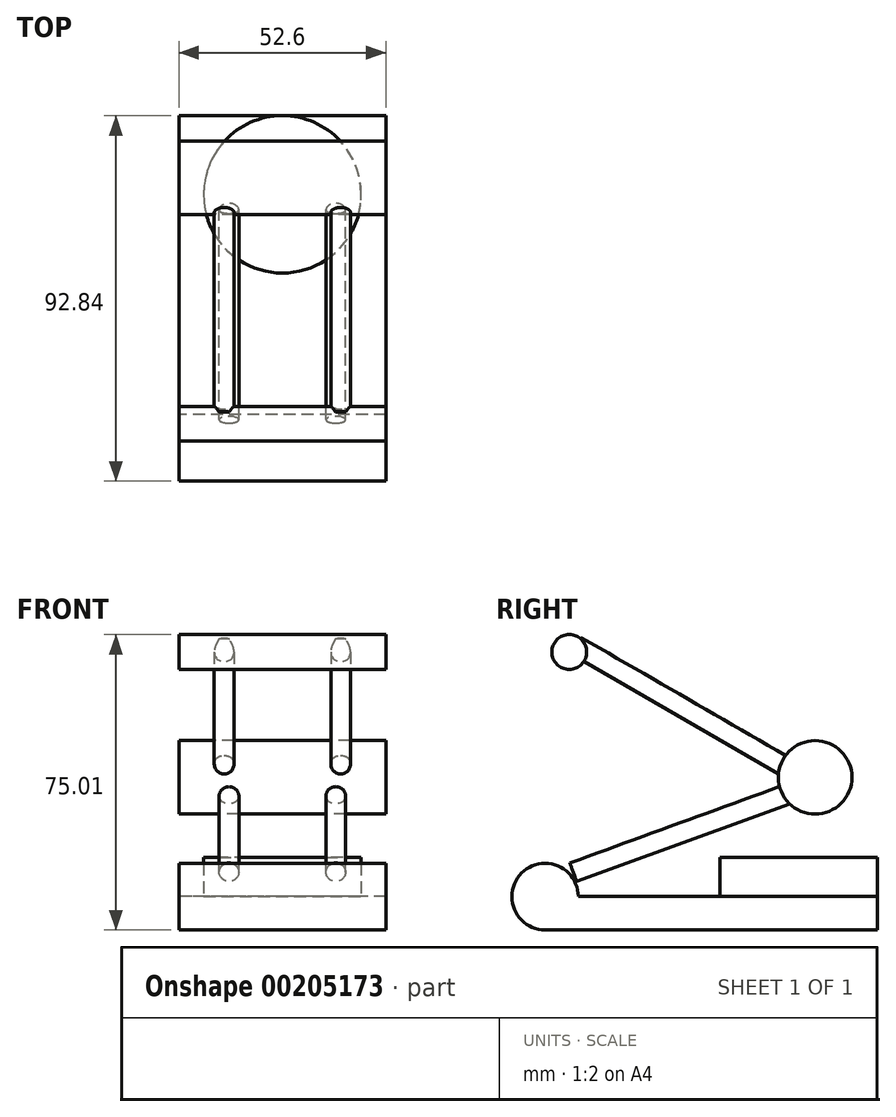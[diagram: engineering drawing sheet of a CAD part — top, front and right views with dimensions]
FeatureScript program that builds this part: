
annotation { "Feature Type Name" : "Feature", "Feature Type Description" : "" }
export const myFeature = defineFeature(function(context is Context, id is Id, definition is map)
    precondition{}
    {
        {
            var Q0;
            Q0=qCreatedBy(makeId("Right.planeOp"),FACE);
            var sketch = newSketch(context, id + "F0", { "sketchPlane" : qUnion([Q0])});
            skLineSegment(sketch, "E0", {"start": v(41.31, 0) * mm, "end": v(-34.65, 0) * mm});
            skCircle(sketch, "E1", {"center": v(25.51, 30.3) * mm, "radius": 9.34 * mm});
            skCircle(sketch, "E2", {"center": v(-36.95, 62.14) * mm, "radius": 4.43 * mm});
            skArc(sketch, "E3", {"start": v(-34.65, 0) * mm, "mid": v(-49.06, 5.97) * mm, "end": v(-43.09, -8.44) * mm});
            skLineSegment(sketch, "E4", {"start": v(41.31, 0) * mm, "end": v(41.31, -8.44) * mm});
            skLineSegment(sketch, "E5", {"start": v(41.31, -8.44) * mm, "end": v(-43.09, -8.44) * mm});
            skSolve(sketch);
        }
        {
            var Q0;
            Q0 = qSketchRegion(id + "F0", true);
            extrude(context, id + "F1", {"entities" : qUnion([Q0]), "endBound" : BoundingType.SYMMETRIC, "depth" : 52.6 * mm});
        }
        {
            var Q0;
            Q0=qCreatedBy(makeId("Front.planeOp"),FACE);
            var Q1;
            Q1=makeQuery(id+"F1.opExtrude","SWEPT_FACE",FACE,{"disambiguationData":[OSD([sQuery(id+"F0.wireOp",EDGE,"E1")])]});
            cPlane(context, id + "F2", {"entities" : qUnion([Q0, Q1]), "cplaneType" : CPlaneType.LINE_ANGLE, "offset" : 25 * mm, "angle" : 30 * degree, "width" : 150 * mm, "height" : 150 * mm});
        }
        {
            var Q0;
            Q0=qCreatedBy(id+"F2.planeOp",FACE);
            var sketch = newSketch(context, id + "F3", { "sketchPlane" : qUnion([Q0])});
            skCircle(sketch, "E6", {"center": v(-14.8, 37.56) * mm, "radius": 2.5 * mm});
            skCircle(sketch, "E7.MirrorC", {"center": v(14.8, 37.56) * mm, "radius": 2.5 * mm});
            skSolve(sketch);
        }
        {
            var Q0;
            Q0 = qSketchRegion(id + "F3", true);
            extrude(context, id + "F4", {"entities" : qUnion([Q0]), "operationType" : NewBodyOperationType.ADD, "oppositeDirection" : true, "depth" : 69.1 * mm});
        }
        {
            var Q0;
            Q0=makeQuery(id+"F1.opExtrude","SWEPT_FACE",FACE,{"disambiguationData":[OSD([sQuery(id+"F0.wireOp",EDGE,"E0")])]});
            var sketch = newSketch(context, id + "F5", { "sketchPlane" : qUnion([Q0])});
            skCircle(sketch, "E8", {"center": v(0, 21.31) * mm, "radius": 20 * mm});
            skSolve(sketch);
        }
        {
            var Q0;
            Q0 = qSketchRegion(id + "F5", true);
            extrude(context, id + "F6", {"entities" : qUnion([Q0]), "operationType" : NewBodyOperationType.ADD, "depth" : 10 * mm});
        }
        {
            var Q0;
            Q0=qCreatedBy(id+"F2.planeOp",FACE);
            var Q1;
            Q1=makeQuery(id+"F1.opExtrude","SWEPT_FACE",FACE,{"disambiguationData":[OSD([sQuery(id+"F0.wireOp",EDGE,"E1")])]});
            cPlane(context, id + "F7", {"entities" : qUnion([Q0, Q1]), "cplaneType" : CPlaneType.LINE_ANGLE, "offset" : 25 * mm, "angle" : 130 * degree, "width" : 150 * mm, "height" : 150 * mm});
        }
        {
            var Q0;
            Q0=qCreatedBy(id+"F7.planeOp",FACE);
            var sketch = newSketch(context, id + "F8", { "sketchPlane" : qUnion([Q0])});
            skCircle(sketch, "E9", {"center": v(13.56, 18.12) * mm, "radius": 2.5 * mm});
            skCircle(sketch, "E10.MirrorC", {"center": v(-13.56, 18.12) * mm, "radius": 2.5 * mm});
            skSolve(sketch);
        }
        {
            var Q0;
            Q0 = qSketchRegion(id + "F8", true);
            extrude(context, id + "F9", {"entities" : qUnion([Q0]), "operationType" : NewBodyOperationType.ADD, "oppositeDirection" : true, "depth" : 66 * mm});
        }
    });
